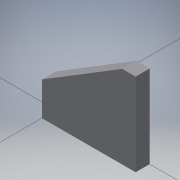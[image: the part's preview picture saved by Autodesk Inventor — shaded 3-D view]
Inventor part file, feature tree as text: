
AUTODESK INVENTOR PART (.ipt)
format: ipt  version: 2019 (Build 230136000, 136)  size: 110,592 bytes
history: native  units: mm
features: sketch x5, other x4, extrude x3, reference x3
ambient origin geometry x8: Origin, YZ Plane, XZ Plane, XY Plane, X Axis, Y Axis, Z Axis, Center Point
bodies: Body1 (feature_tree)
feature tree (15):
  other  "Твердое тело1"
  extrude  "Выдавливание1"  Depth=20.0mm
  extrude  "Выдавливание2"  Depth=6.0mm TaperAngle=0.0deg
  extrude  "Выдавливание3"  Depth=6.0mm TaperAngle=0.0deg
  sketch  "Эскиз4"
  sketch  "Эскиз5"
  sketch  "Эскиз1"
  reference  "Ссылка1"
  sketch  "Эскиз2"
  sketch  "Эскиз3"
  reference  "Ссылка2"
  reference  "Ссылка3"
  parser-record x1  (decoder bookkeeping rows leaked as tree rows — omitted from the tree; the rows remain in map.json)
  other  "kowsh.iam"
  other  "Барабан:1"
note: 1 file-system path scrubbed to <path> (originals preserved in map.json)
